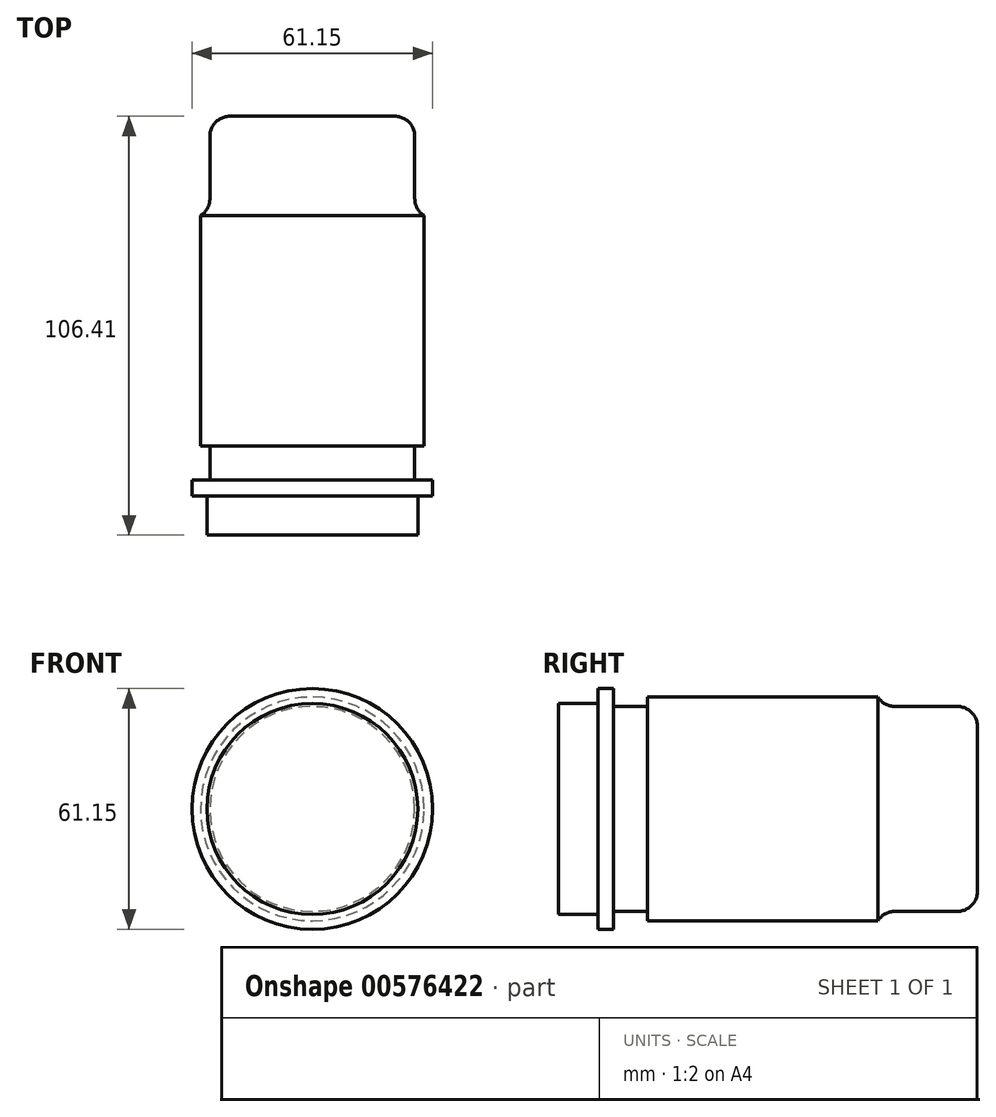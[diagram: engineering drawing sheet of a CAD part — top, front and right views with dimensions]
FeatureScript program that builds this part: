
annotation { "Feature Type Name" : "Feature", "Feature Type Description" : "" }
export const myFeature = defineFeature(function(context is Context, id is Id, definition is map)
    precondition{}
    {
        {
            var Q0;
            Q0=qCreatedBy(makeId("Front.planeOp"),FACE);
            var sketch = newSketch(context, id + "F0", { "sketchPlane" : qUnion([Q0])});
            skCircle(sketch, "E0", {"center": v(-20.67, -15.8) * mm, "radius": 26.02 * mm});
            skPoint(sketch, "E0.first.point", {"position": v(0, 0) * mm});
            skPoint(sketch, "E0.second.point", {"position": v(-28.64, -40.58) * mm});
            skPoint(sketch, "E0.third.point", {"position": v(-43.6, -28.1) * mm});
            skSolve(sketch);
        }
        {
            var Q0;
            Q0=makeQuery(id+"F0.imprint","IMPRINT",FACE,{"disambiguationData":[TD([[makeQuery(id+"F0.imprint","IMPRINT",EDGE,{"derivedFrom":sQuery(id+"F0.wireOp",EDGE,"E0")}),1.0]])]});
            extrude(context, id + "F1", {"entities" : qUnion([Q0]), "depth" : 74.12 * mm, "offsetDistance" : 25.4 * mm, "hasSecondDirection" : true, "secondDirectionOppositeDirection" : true, "secondDirectionDepth" : 18.35 * mm});
        }
        {
            var Q0;
            Q0=makeQuery(id+"F1.opExtrude","CAP_FACE",FACE,{"disambiguationData":[OSD([sQuery(id+"F0.wireOp",EDGE,"E0")])],"isStart":false});
            var sketch = newSketch(context, id + "F2", { "sketchPlane" : qUnion([Q0])});
            skCircle(sketch, "E1", {"center": v(-20.67, -15.8) * mm, "radius": 28.4 * mm});
            skSolve(sketch);
        }
        {
            var Q0;
            Q0 = qSketchRegion(id + "F2", true);
            extrude(context, id + "F3", {"entities" : qUnion([Q0]), "operationType" : NewBodyOperationType.ADD, "oppositeDirection" : true, "depth" : 67.2 * mm, "offsetDistance" : 25.4 * mm, "hasSecondDirection" : true, "secondDirectionOppositeDirection" : true, "secondDirectionDepth" : 8.67 * mm});
        }
        {
            var Q0;
            Q0=makeQuery(id+"F1.opExtrude","CAP_FACE",FACE,{"disambiguationData":[OSD([sQuery(id+"F0.wireOp",EDGE,"E0")])],"isStart":true});
            var Q1;
            {var subQ0=sQuery(id+"F0.wireOp",EDGE,"E0");Q1=makeQuery(id+"F3.boolean.opBoolean","SPLIT",FACE,{"disambiguationData":[TD([makeQuery(id+"F1.opExtrude","CAP_FACE",FACE,{"disambiguationData":[OSD([subQ0])],"isStart":true})])],"derivedFrom":makeQuery(id+"F1.opExtrude","SWEPT_FACE",FACE,{"disambiguationData":[OSD([subQ0])]})});}
            fillet(context, id + "F4", {"entities" : qUnion([Q0, Q1]), "radius" : 5.08 * mm, "tangentPropagation" : true, "allowEdgeOverflow" : false});
        }
        {
            var Q0;
            Q0=makeQuery(id+"F1.opExtrude","CAP_FACE",FACE,{"disambiguationData":[OSD([sQuery(id+"F0.wireOp",EDGE,"E0")])],"isStart":false});
            var sketch = newSketch(context, id + "F5", { "sketchPlane" : qUnion([Q0])});
            skCircle(sketch, "E2", {"center": v(-20.67, -15.8) * mm, "radius": 30.58 * mm});
            skSolve(sketch);
        }
        {
            var Q0;
            Q0=makeQuery(id+"F5.imprint","IMPRINT",FACE,{"disambiguationData":[TD([[makeQuery(id+"F5.imprint","IMPRINT",EDGE,{"derivedFrom":makeQuery(id+"F1.opExtrude","CAP_EDGE",EDGE,{"disambiguationData":[OSD([sQuery(id+"F0.wireOp",EDGE,"E0")])],"isStart":false})}),1.0]])]});
            var Q1;
            Q1 = qSketchRegion(id + "F5", true);
            extrude(context, id + "F6", {"entities" : qUnion([Q0, Q1]), "operationType" : NewBodyOperationType.ADD, "depth" : 3.96 * mm, "offsetDistance" : 25.4 * mm});
        }
        {
            var Q0;
            Q0=makeQuery(id+"F6.opExtrude","CAP_FACE",FACE,{"disambiguationData":[OSD([sQuery(id+"F5.wireOp",EDGE,"E2")])],"isStart":false});
            var sketch = newSketch(context, id + "F7", { "sketchPlane" : qUnion([Q0])});
            skCircle(sketch, "E3", {"center": v(-20.67, -15.8) * mm, "radius": 26.8 * mm});
            skSolve(sketch);
        }
        {
            var Q0;
            Q0 = qSketchRegion(id + "F7", true);
            extrude(context, id + "F8", {"entities" : qUnion([Q0]), "operationType" : NewBodyOperationType.ADD, "depth" : 9.98 * mm, "offsetDistance" : 25.4 * mm});
        }
    });
